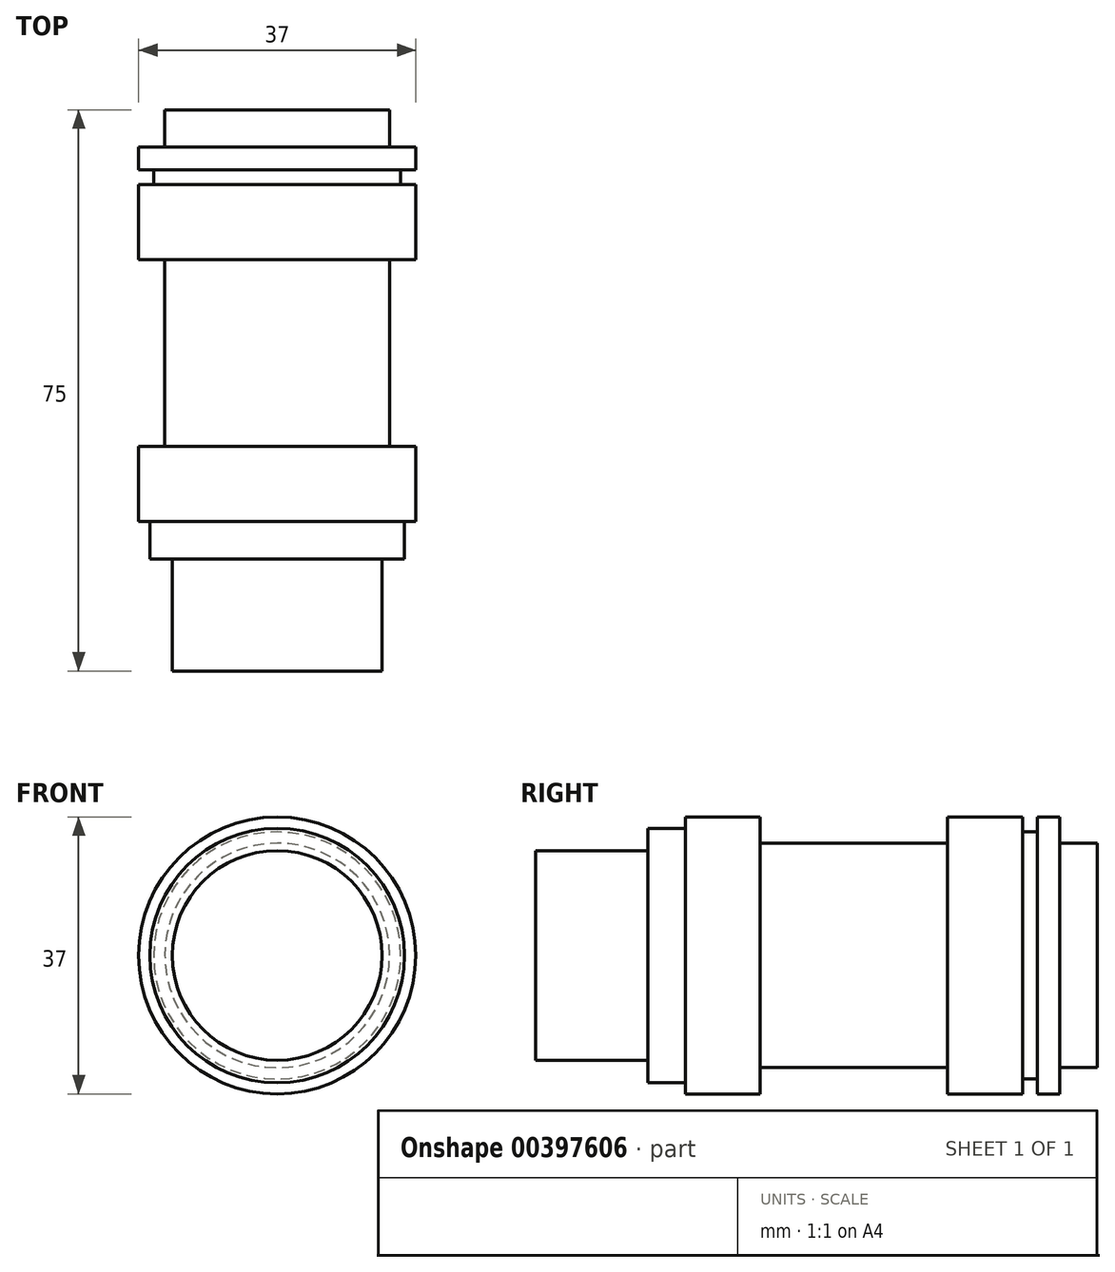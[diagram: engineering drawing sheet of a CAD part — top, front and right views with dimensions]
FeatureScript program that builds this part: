
annotation { "Feature Type Name" : "Feature", "Feature Type Description" : "" }
export const myFeature = defineFeature(function(context is Context, id is Id, definition is map)
    precondition{}
    {
        {
            var Q0;
            Q0=qCreatedBy(makeId("Front.planeOp"),FACE);
            var sketch = newSketch(context, id + "F0", { "sketchPlane" : qUnion([Q0])});
            skCircle(sketch, "E0", {"center": v(0, 0) * mm, "radius": 17 * mm});
            skSolve(sketch);
        }
        {
            var Q0;
            Q0=qSketchRegion(id+"F0",true);
            extrude(context, id + "F1", {"entities" : qUnion([Q0]), "depth" : 5 * mm});
        }
        {
            var Q0;
            Q0=makeQuery(id+"F1.opExtrude","CAP_FACE",FACE,{"disambiguationData":[OSD([sQuery(id+"F0.wireOp",EDGE,"E0")])],"isStart":false});
            var sketch = newSketch(context, id + "F2", { "sketchPlane" : qUnion([Q0])});
            skCircle(sketch, "E1", {"center": v(0, 0) * mm, "radius": 14 * mm});
            skSolve(sketch);
        }
        {
            var Q0;
            Q0=qSketchRegion(id+"F2",true);
            extrude(context, id + "F3", {"entities" : qUnion([Q0]), "operationType" : NewBodyOperationType.ADD, "depth" : 15 * mm});
        }
        {
            var Q0;
            Q0=qCreatedBy(makeId("Front.planeOp"),FACE);
            var sketch = newSketch(context, id + "F4", { "sketchPlane" : qUnion([Q0])});
            skCircle(sketch, "E2", {"center": v(0, 0) * mm, "radius": 18.5 * mm});
            skSolve(sketch);
        }
        {
            var Q0;
            Q0=qSketchRegion(id+"F4",true);
            extrude(context, id + "F5", {"entities" : qUnion([Q0]), "operationType" : NewBodyOperationType.ADD, "oppositeDirection" : true, "depth" : 10 * mm});
        }
        {
            var Q0;
            Q0=qCreatedBy(makeId("Front.planeOp"),FACE);
            var sketch = newSketch(context, id + "F6", { "sketchPlane" : qUnion([Q0])});
            skCircle(sketch, "E3", {"center": v(0, 0) * mm, "radius": 15 * mm});
            skSolve(sketch);
        }
        {
            var Q0;
            Q0=qSketchRegion(id+"F6",true);
            extrude(context, id + "F7", {"entities" : qUnion([Q0]), "operationType" : NewBodyOperationType.ADD, "oppositeDirection" : true, "depth" : 35 * mm});
        }
        {
            var Q0;
            Q0=makeQuery(id+"F7.opExtrude","CAP_FACE",FACE,{"disambiguationData":[OSD([sQuery(id+"F6.wireOp",EDGE,"E3")])],"isStart":false});
            var sketch = newSketch(context, id + "F8", { "sketchPlane" : qUnion([Q0])});
            skCircle(sketch, "E4", {"center": v(0, 0) * mm, "radius": 18.5 * mm});
            skSolve(sketch);
        }
        {
            var Q0;
            Q0=qSketchRegion(id+"F8",true);
            extrude(context, id + "F9", {"entities" : qUnion([Q0]), "operationType" : NewBodyOperationType.ADD, "depth" : 10 * mm});
        }
        {
            var Q0;
            Q0=makeQuery(id+"F9.opExtrude","CAP_FACE",FACE,{"disambiguationData":[OSD([sQuery(id+"F8.wireOp",EDGE,"E4")])],"isStart":false});
            var sketch = newSketch(context, id + "F10", { "sketchPlane" : qUnion([Q0])});
            skCircle(sketch, "E5", {"center": v(0, 0) * mm, "radius": 16.5 * mm});
            skSolve(sketch);
        }
        {
            var Q0;
            Q0=qSketchRegion(id+"F10",true);
            extrude(context, id + "F11", {"entities" : qUnion([Q0]), "operationType" : NewBodyOperationType.ADD, "depth" : 2 * mm});
        }
        {
            var Q0;
            Q0=makeQuery(id+"F11.opExtrude","CAP_FACE",FACE,{"disambiguationData":[OSD([sQuery(id+"F10.wireOp",EDGE,"E5")])],"isStart":false});
            var sketch = newSketch(context, id + "F12", { "sketchPlane" : qUnion([Q0])});
            skCircle(sketch, "E6", {"center": v(0, 0) * mm, "radius": 18.5 * mm});
            skSolve(sketch);
        }
        {
            var Q0;
            Q0=qSketchRegion(id+"F12",true);
            extrude(context, id + "F13", {"entities" : qUnion([Q0]), "operationType" : NewBodyOperationType.ADD, "depth" : 3 * mm});
        }
        {
            var Q0;
            Q0=makeQuery(id+"F13.opExtrude","CAP_FACE",FACE,{"disambiguationData":[OSD([sQuery(id+"F12.wireOp",EDGE,"E6")])],"isStart":false});
            var sketch = newSketch(context, id + "F14", { "sketchPlane" : qUnion([Q0])});
            skCircle(sketch, "E7", {"center": v(0, 0) * mm, "radius": 15 * mm});
            skSolve(sketch);
        }
        {
            var Q0;
            Q0=qSketchRegion(id+"F14",true);
            extrude(context, id + "F15", {"entities" : qUnion([Q0]), "operationType" : NewBodyOperationType.ADD, "depth" : 5 * mm});
        }
    });
